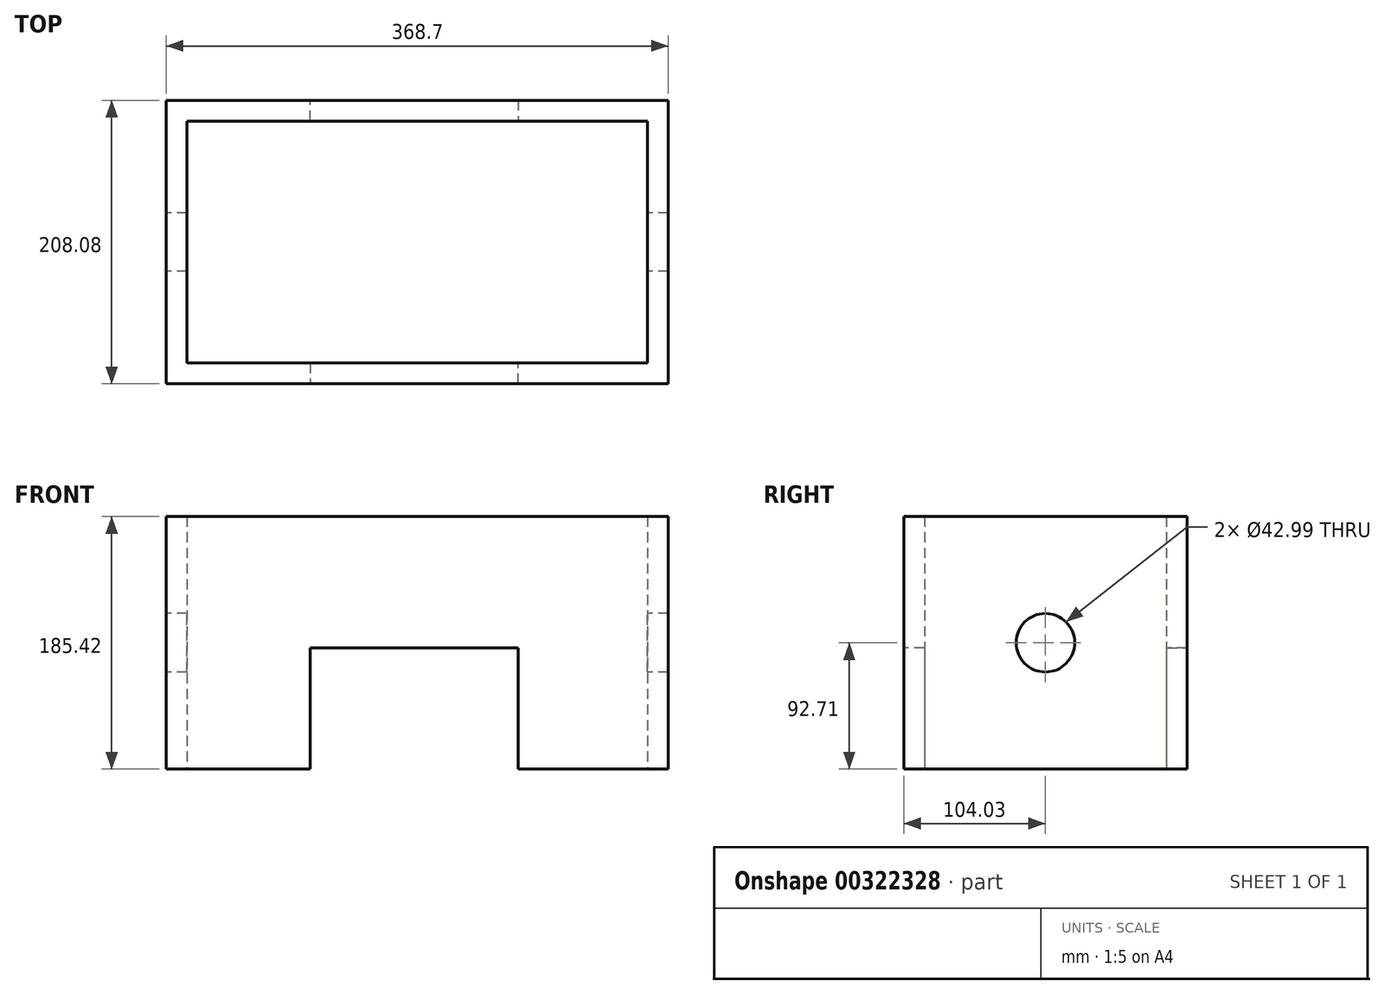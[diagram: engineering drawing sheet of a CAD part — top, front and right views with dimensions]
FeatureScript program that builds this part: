
annotation { "Feature Type Name" : "Feature", "Feature Type Description" : "" }
export const myFeature = defineFeature(function(context is Context, id is Id, definition is map)
    precondition{}
    {
        {
            var Q0;
            Q0=qCreatedBy(makeId("Top.planeOp"),FACE);
            var sketch = newSketch(context, id + "F0", { "sketchPlane" : qUnion([Q0])});
            skLineSegment(sketch, "E0.bottom", {"start": v(-181.71, 104.05) * mm, "end": v(187, 104.05) * mm});
            skLineSegment(sketch, "E0.top", {"start": v(-181.71, -104.03) * mm, "end": v(187, -104.03) * mm});
            skLineSegment(sketch, "E0.left", {"start": v(-181.71, 104.05) * mm, "end": v(-181.71, -104.03) * mm});
            skLineSegment(sketch, "E0.right", {"start": v(187, 104.05) * mm, "end": v(187, -104.03) * mm});
            skLineSegment(sketch, "E1.bottom", {"start": v(-166.47, 88.8) * mm, "end": v(171.75, 88.8) * mm});
            skLineSegment(sketch, "E1.top", {"start": v(-166.47, -88.79) * mm, "end": v(171.75, -88.79) * mm});
            skLineSegment(sketch, "E1.left", {"start": v(-166.47, 88.8) * mm, "end": v(-166.47, -88.79) * mm});
            skLineSegment(sketch, "E1.right", {"start": v(171.75, 88.8) * mm, "end": v(171.75, -88.79) * mm});
            skSolve(sketch);
        }
        {
            var Q0;
            Q0=makeQuery(id+"F0.imprint","IMPRINT",FACE,{"disambiguationData":[TD([[makeQuery(id+"F0.imprint","IMPRINT",EDGE,{"derivedFrom":sQuery(id+"F0.wireOp",EDGE,"E0.bottom")}),-1.0]])]});
            extrude(context, id + "F1", {"entities" : qUnion([Q0]), "depth" : 185.42 * mm});
        }
        {
            var Q0;
            Q0=qCreatedBy(makeId("Top.planeOp"),FACE);
            var sketch = newSketch(context, id + "F2", { "sketchPlane" : qUnion([Q0])});
            skLineSegment(sketch, "E2.bottom", {"start": v(-76.5, 75.47) * mm, "end": v(75.9, 75.47) * mm});
            skLineSegment(sketch, "E2.top", {"start": v(-76.5, -76.93) * mm, "end": v(75.9, -76.93) * mm});
            skLineSegment(sketch, "E2.left", {"start": v(-76.5, 75.47) * mm, "end": v(-76.5, -76.93) * mm});
            skLineSegment(sketch, "E2.right", {"start": v(75.9, 75.47) * mm, "end": v(75.9, -76.93) * mm});
            skSolve(sketch);
        }
        {
            var Q0;
            Q0=makeQuery(id+"F2.imprint","IMPRINT",FACE,{"disambiguationData":[TD([[makeQuery(id+"F2.imprint","IMPRINT",EDGE,{"derivedFrom":sQuery(id+"F2.wireOp",EDGE,"E2.bottom")}),-1.0]])]});
            var sketch = newSketch(context, id + "F3", { "sketchPlane" : qUnion([Q0])});
            skLineSegment(sketch, "E3", {"start": v(-75.86, -76.92) * mm, "end": v(-75.86, -88.61) * mm});
            skLineSegment(sketch, "E4", {"start": v(-75.86, -88.61) * mm, "end": v(-75.86, -103.53) * mm});
            skLineSegment(sketch, "E5", {"start": v(-75.86, -103.53) * mm, "end": v(76.54, -103.53) * mm});
            skLineSegment(sketch, "E6", {"start": v(76.54, -103.53) * mm, "end": v(76.54, -88.61) * mm});
            skLineSegment(sketch, "E7", {"start": v(76.54, -88.61) * mm, "end": v(-75.86, -88.61) * mm});
            skLineSegment(sketch, "E8", {"start": v(-76.13, 75.52) * mm, "end": v(-76.13, 89.14) * mm});
            skLineSegment(sketch, "E9", {"start": v(-76.13, 89.14) * mm, "end": v(-76.13, 104.03) * mm});
            skLineSegment(sketch, "E10", {"start": v(-76.13, 104.03) * mm, "end": v(76.66, 104.03) * mm});
            skLineSegment(sketch, "E11", {"start": v(76.66, 104.03) * mm, "end": v(76.66, 88.85) * mm});
            skLineSegment(sketch, "E12", {"start": v(76.66, 88.85) * mm, "end": v(-76.13, 89.14) * mm});
            skSolve(sketch);
        }
        {
            var Q0;
            Q0=makeQuery(id+"F3.imprint","IMPRINT",FACE,{"disambiguationData":[TD([[makeQuery(id+"F3.imprint","IMPRINT",EDGE,{"derivedFrom":sQuery(id+"F3.wireOp",EDGE,"E4")}),1.0]])]});
            var Q1;
            Q1=makeQuery(id+"F3.imprint","IMPRINT",FACE,{"disambiguationData":[TD([[makeQuery(id+"F3.imprint","IMPRINT",EDGE,{"derivedFrom":sQuery(id+"F3.wireOp",EDGE,"E9")}),-1.0]])]});
            extrude(context, id + "F4", {"entities" : qUnion([Q0, Q1]), "operationType" : NewBodyOperationType.REMOVE, "depth" : 88.9 * mm});
        }
        {
            var Q0;
            Q0=makeQuery(id+"F4.boolean.opBoolean","COPY",FACE,{"derivedFrom":makeQuery(id+"F4.opExtrude","SWEPT_FACE",FACE,{"disambiguationData":[OSD([sQuery(id+"F3.wireOp",EDGE,"E5")])]})});
            extrude(context, id + "F5", {"entities" : qUnion([Q0]), "operationType" : NewBodyOperationType.REMOVE, "oppositeDirection" : true, "depth" : 14.22 * mm});
        }
        {
            var Q0;
            Q0=makeQuery(id+"F4.boolean.opBoolean","COPY",FACE,{"derivedFrom":makeQuery(id+"F4.opExtrude","SWEPT_FACE",FACE,{"disambiguationData":[OSD([sQuery(id+"F3.wireOp",EDGE,"E12")])]})});
            extrude(context, id + "F6", {"entities" : qUnion([Q0]), "operationType" : NewBodyOperationType.REMOVE, "oppositeDirection" : true, "depth" : 25.4 * mm});
        }
        {
            var Q0;
            Q0=makeQuery(id+"F4.boolean.opBoolean","COPY",FACE,{"derivedFrom":makeQuery(id+"F4.opExtrude","SWEPT_FACE",FACE,{"disambiguationData":[OSD([sQuery(id+"F3.wireOp",EDGE,"E10")])]})});
            extrude(context, id + "F7", {"entities" : qUnion([Q0]), "operationType" : NewBodyOperationType.REMOVE, "oppositeDirection" : true, "depth" : 25.4 * mm});
        }
        {
            var Q0;
            Q0=makeQuery(id+"F1.opExtrude","SWEPT_FACE",FACE,{"disambiguationData":[OSD([sQuery(id+"F0.wireOp",EDGE,"E0.left")])]});
            var sketch = newSketch(context, id + "F8", { "sketchPlane" : qUnion([Q0])});
            skCircle(sketch, "E13", {"center": v(0, 92.71) * mm, "radius": 21.5 * mm});
            skPoint(sketch, "E13.centerSnap0", {"position": v(-104.05, 92.71) * mm});
            skSolve(sketch);
        }
        {
            var Q0;
            Q0=makeQuery(id+"F8.imprint","IMPRINT",FACE,{"disambiguationData":[TD([[makeQuery(id+"F8.imprint","IMPRINT",EDGE,{"derivedFrom":sQuery(id+"F8.wireOp",EDGE,"E13")}),1.0]])]});
            extrude(context, id + "F9", {"entities" : qUnion([Q0]), "operationType" : NewBodyOperationType.REMOVE, "oppositeDirection" : true, "depth" : 469.9 * mm});
        }
    });
